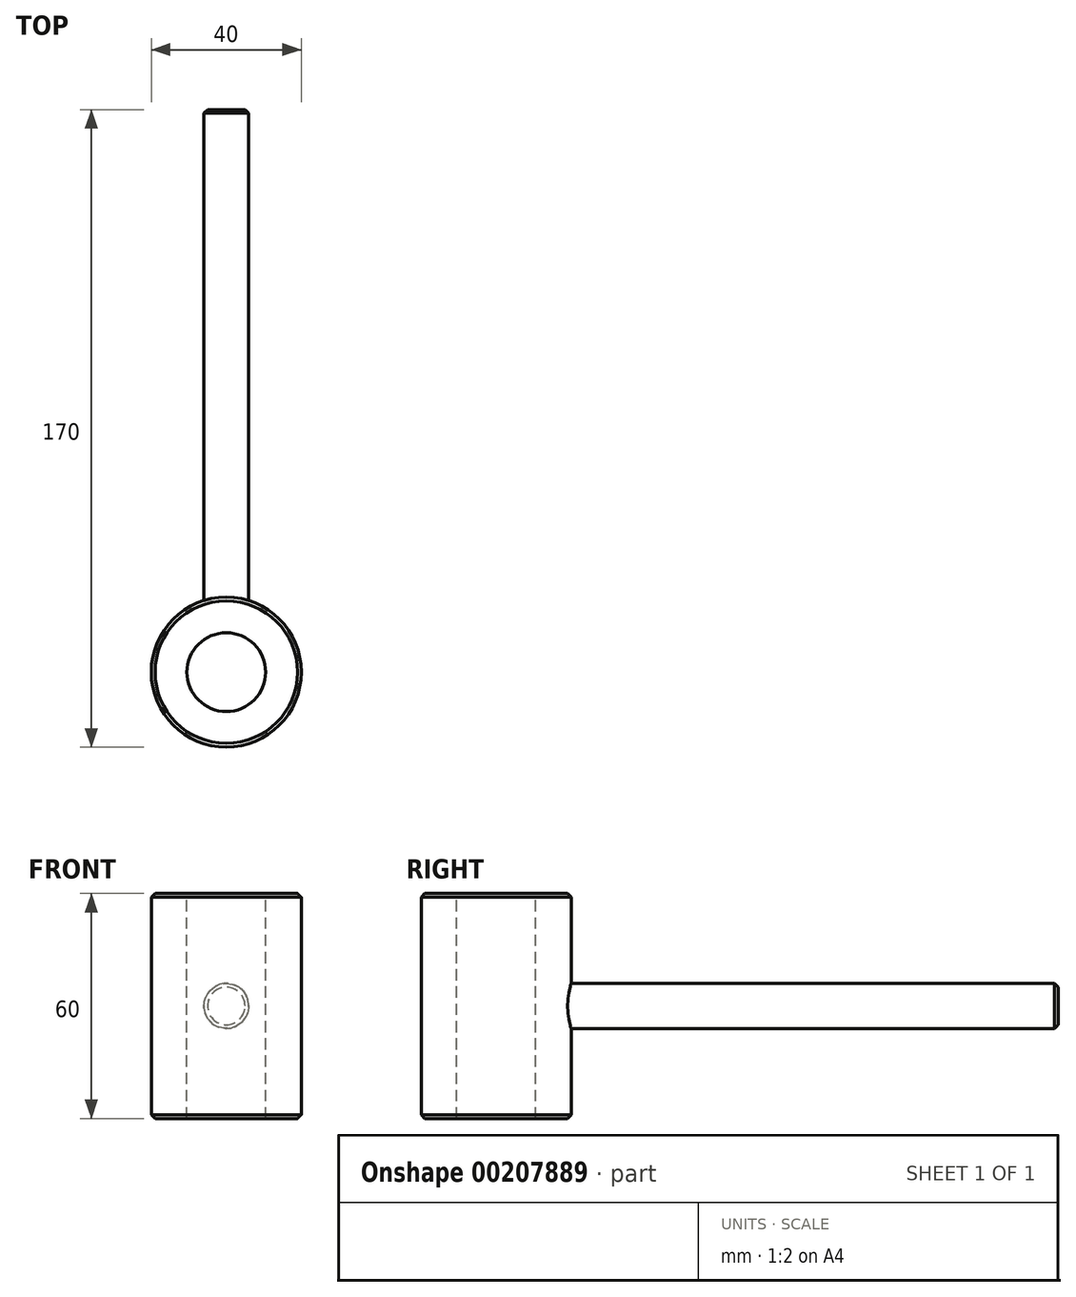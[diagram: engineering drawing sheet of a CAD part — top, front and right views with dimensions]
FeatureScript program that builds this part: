
annotation { "Feature Type Name" : "Feature", "Feature Type Description" : "" }
export const myFeature = defineFeature(function(context is Context, id is Id, definition is map)
    precondition{}
    {
        {
            var Q0;
            Q0=qCreatedBy(makeId("Top.planeOp"),FACE);
            var sketch = newSketch(context, id + "F0", { "sketchPlane" : qUnion([Q0])});
            skCircle(sketch, "E0", {"center": v(0, 0) * mm, "radius": 20 * mm});
            skSolve(sketch);
        }
        {
            var Q0;
            Q0 = qSketchRegion(id + "F0", true);
            extrude(context, id + "F1", {"entities" : qUnion([Q0]), "depth" : 60 * mm, "symmetric" : true});
        }
        {
            var Q0;
            Q0=makeQuery(id+"F1.opExtrude","CAP_FACE",FACE,{"disambiguationData":[OSD([sQuery(id+"F0.wireOp",EDGE,"E0")])],"isStart":false});
            var sketch = newSketch(context, id + "F2", { "sketchPlane" : qUnion([Q0])});
            skPoint(sketch, "E1", {"position": v(0, 0) * mm});
            skSolve(sketch);
        }
        {
            var Q0;
            Q0=sQuery(id+"F2.wireOp",VERTEX,"E1");
            var Q1;
            Q1=makeQuery(id+"F1.opExtrude","SWEPT_BODY",BODY,{"disambiguationData":[OSD([sQuery(id+"F0.wireOp",EDGE,"E0")])]});
            hole(context, id + "F3", {"style" : HoleStyle.SIMPLE, "endStyle" : HoleEndStyle.THROUGH, "holeDiameter" : 21 * mm, "startFromSketch" : true, "locations" : qUnion([Q0]), "scope" : qUnion([Q1]), "isTappedThrough" : true});
        }
        {
            var Q0;
            Q0=qCreatedBy(makeId("Front.planeOp"),FACE);
            cPlane(context, id + "F4", {"entities" : qUnion([Q0]), "cplaneType" : CPlaneType.OFFSET, "offset" : 150 * mm, "oppositeDirection" : true, "width" : 150 * mm, "height" : 150 * mm});
        }
        {
            var Q0;
            Q0=qCreatedBy(id+"F4.planeOp",FACE);
            var sketch = newSketch(context, id + "F5", { "sketchPlane" : qUnion([Q0])});
            skCircle(sketch, "E2", {"center": v(0, 0) * mm, "radius": 6 * mm});
            skSolve(sketch);
        }
        {
            var Q0;
            Q0=makeQuery(id+"F5.imprint","IMPRINT",FACE,{"disambiguationData":[TD([[makeQuery(id+"F5.imprint","IMPRINT",EDGE,{"derivedFrom":sQuery(id+"F5.wireOp",EDGE,"E2")}),1.0]])]});
            var Q1;
            Q1=makeQuery(id+"F1.opExtrude","SWEPT_FACE",FACE,{"disambiguationData":[OSD([sQuery(id+"F0.wireOp",EDGE,"E0")])]});
            extrude(context, id + "F6", {"entities" : qUnion([Q0]), "operationType" : NewBodyOperationType.ADD, "endBound" : BoundingType.UP_TO_SURFACE, "endBoundEntityFace" : qUnion([Q1]), "depth" : 25 * mm});
        }
        {
            var Q0;
            Q0=makeQuery(id+"F6.opExtrude","CAP_EDGE",EDGE,{"disambiguationData":[OSD([sQuery(id+"F5.wireOp",EDGE,"E2")])],"isStart":true});
            var Q1;
            Q1=makeQuery(id+"F1.opExtrude","CAP_EDGE",EDGE,{"disambiguationData":[OSD([sQuery(id+"F0.wireOp",EDGE,"E0")])],"isStart":false});
            var Q2;
            Q2=makeQuery(id+"F3.hole-0.boolean.opBoolean","COPY",EDGE,{"derivedFrom":makeQuery(id+"F3.hole-0.opRevolve","SWEPT_EDGE",EDGE,{"disambiguationData":[OSD([sQuery(id+"F3.hole-0.sketch.wireOp",EDGE,"core_line_2"),sQuery(id+"F3.hole-0.sketch.wireOp",EDGE,"core_line_3")])]})});
            var Q3;
            Q3=makeQuery(id+"F1.opExtrude","CAP_EDGE",EDGE,{"disambiguationData":[OSD([sQuery(id+"F0.wireOp",EDGE,"E0")])],"isStart":true});
            var Q4;
            Q4=makeQuery(id+"F3.hole-0.boolean.opBoolean","INTERSECT",EDGE,{"derivedFrom":[makeQuery(id+"F1.opExtrude","CAP_FACE",FACE,{"disambiguationData":[OSD([sQuery(id+"F0.wireOp",EDGE,"E0")])],"isStart":true}),makeQuery(id+"F3.hole-0.opRevolve","SWEPT_FACE",FACE,{"disambiguationData":[OSD([sQuery(id+"F3.hole-0.sketch.wireOp",EDGE,"core_line_2")])]})]});
            chamfer(context, id + "F7", {"entities" : qUnion([Q0, Q1, Q2, Q3, Q4]), "width" : 1 * mm, "tangentPropagation" : true});
        }
    });
